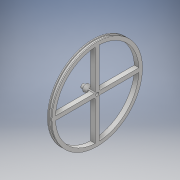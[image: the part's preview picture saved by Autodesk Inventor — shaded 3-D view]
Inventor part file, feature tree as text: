
AUTODESK INVENTOR PART (.ipt)
format: ipt  version: 2018 (Build 220112000, 112)  size: 210,432 bytes
history: native  units: mm
features: extrude x12, sketch x12, fillet x2, pattern_circular x1
ambient origin geometry x8: Origin, YZ Plane, XZ Plane, XY Plane, X Axis, Y Axis, Z Axis, Center Point
bodies: Solid1 (feature_tree)
feature tree (27):
  extrude  "Extrusion1"  Depth=3.5mm TaperAngle=0.0deg
  extrude  "Extrusion2"  Depth=1.0mm TaperAngle=0.0deg
  extrude  "Extrusion3"  Depth=1.0mm TaperAngle=0.0deg
  extrude  "Extrusion4"  Depth=6.0mm TaperAngle=0.0deg
  extrude  "Extrusion5"  Depth=10.0mm TaperAngle=0.0deg
  extrude  "Extrusion6"  Depth=1.0mm TaperAngle=0.0deg
  extrude  "Extrusion7"  Depth=1.0mm
  extrude  "Extrusion8"  Depth=10.0mm
  extrude  "Extrusion9"  Depth=40.0mm TaperAngle=360.0deg
  extrude  "Extrusion10"  Depth=2.0mm TaperAngle=0.0deg
  pattern_circular  "Circular Pattern1"  [2 undecoded]
  fillet  "Fillet1"  [1 undecoded]
  extrude  "Extrusion11"  [1 undecoded]
  extrude  "Extrusion12"  [1 undecoded]
  fillet  "Fillet2"  [1 undecoded]
  sketch  "Sketch1"  dims[d0=88.0mm d1=3.5mm d2=0.0mm]
  sketch  "Sketch2"  dims[d3=90.0mm d4=1.0mm d5=0.0mm]
  sketch  "Sketch3"  dims[d6=90.0mm d7=1.0mm d8=0.0mm]
  sketch  "Sketch4"  dims[d9=83.0mm d10=6.0mm d11=0.0mm]
  sketch  "Sketch5"  dims[d12=7.0mm d13=10.0mm d14=0.0mm]
  sketch  "Sketch6"  dims[d15=2.0mm d16=0.0mm d17=1.0mm d18=0.0mm]
  sketch  "Sketch7"  dims[d19=1.0mm d20=0.0mm d21=3.25mm]
  sketch  "Sketch8"  dims[d22=10.0mm d23=0.0mm d24=4.0mm]
  sketch  "Sketch9"  dims[d25=4.5mm d26=0.0mm d27=40.0mm d28=360.0deg]
  sketch  "Sketch10"  dims[d30=2.0mm d31=2.0mm d32=0.0mm]
  sketch  "Sketch11"  dims[d33=4.0mm]
  sketch  "Sketch12"  dims[d34=3.3mm d35=0.0mm d36=0.5mm]
note: 6 required parameter values undecoded (feature->parameter linkage not recoverable at this tier; creation-order binding heuristic only, values carry confidence <= 0.55)
